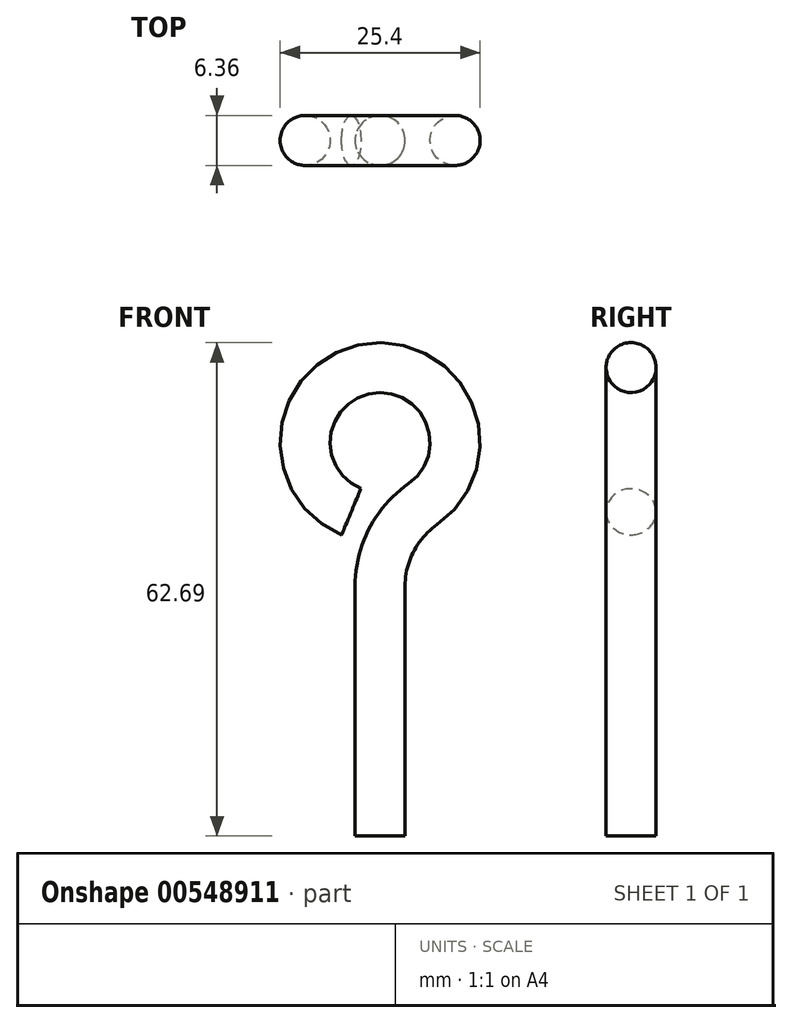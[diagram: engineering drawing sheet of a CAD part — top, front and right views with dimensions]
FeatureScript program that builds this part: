
annotation { "Feature Type Name" : "Feature", "Feature Type Description" : "" }
export const myFeature = defineFeature(function(context is Context, id is Id, definition is map)
    precondition{}
    {
        {
            var Q0;
            Q0=qCreatedBy(makeId("Top.planeOp"),FACE);
            var sketch = newSketch(context, id + "F0", { "sketchPlane" : qUnion([Q0])});
            skCircle(sketch, "E0", {"center": v(0, 0) * mm, "radius": 3.18 * mm});
            skSolve(sketch);
        }
        {
            var Q0;
            Q0=qCreatedBy(makeId("Front.planeOp"),FACE);
            var sketch = newSketch(context, id + "F1", { "sketchPlane" : qUnion([Q0])});
            skLineSegment(sketch, "E1", {"start": v(0, 0) * mm, "end": v(0, 31.75) * mm});
            skArc(sketch, "E2", {"start": v(0, 31.75) * mm, "mid": v(1.44, 37.63) * mm, "end": v(5.44, 42.17) * mm});
            skArc(sketch, "E3", {"start": v(5.44, 42.17) * mm, "mid": v(-1.01, 59.46) * mm, "end": v(-3.66, 41.2) * mm});
            skSolve(sketch);
        }
        {
            var Q0;
            Q0=makeQuery(id+"F0.imprint","IMPRINT",FACE,{"disambiguationData":[TD([[makeQuery(id+"F0.imprint","IMPRINT",EDGE,{"derivedFrom":sQuery(id+"F0.wireOp",EDGE,"E0")}),1.0]])]});
            var Q1;
            Q1=sQuery(id+"F1.wireOp",EDGE,"E1");
            var Q2;
            Q2=sQuery(id+"F1.wireOp",EDGE,"E2");
            var Q3;
            Q3=sQuery(id+"F1.wireOp",EDGE,"E3");
            sweep(context, id + "F2", {"profiles" : qUnion([Q0]), "path" : qUnion([Q1, Q2, Q3])});
        }
    });
